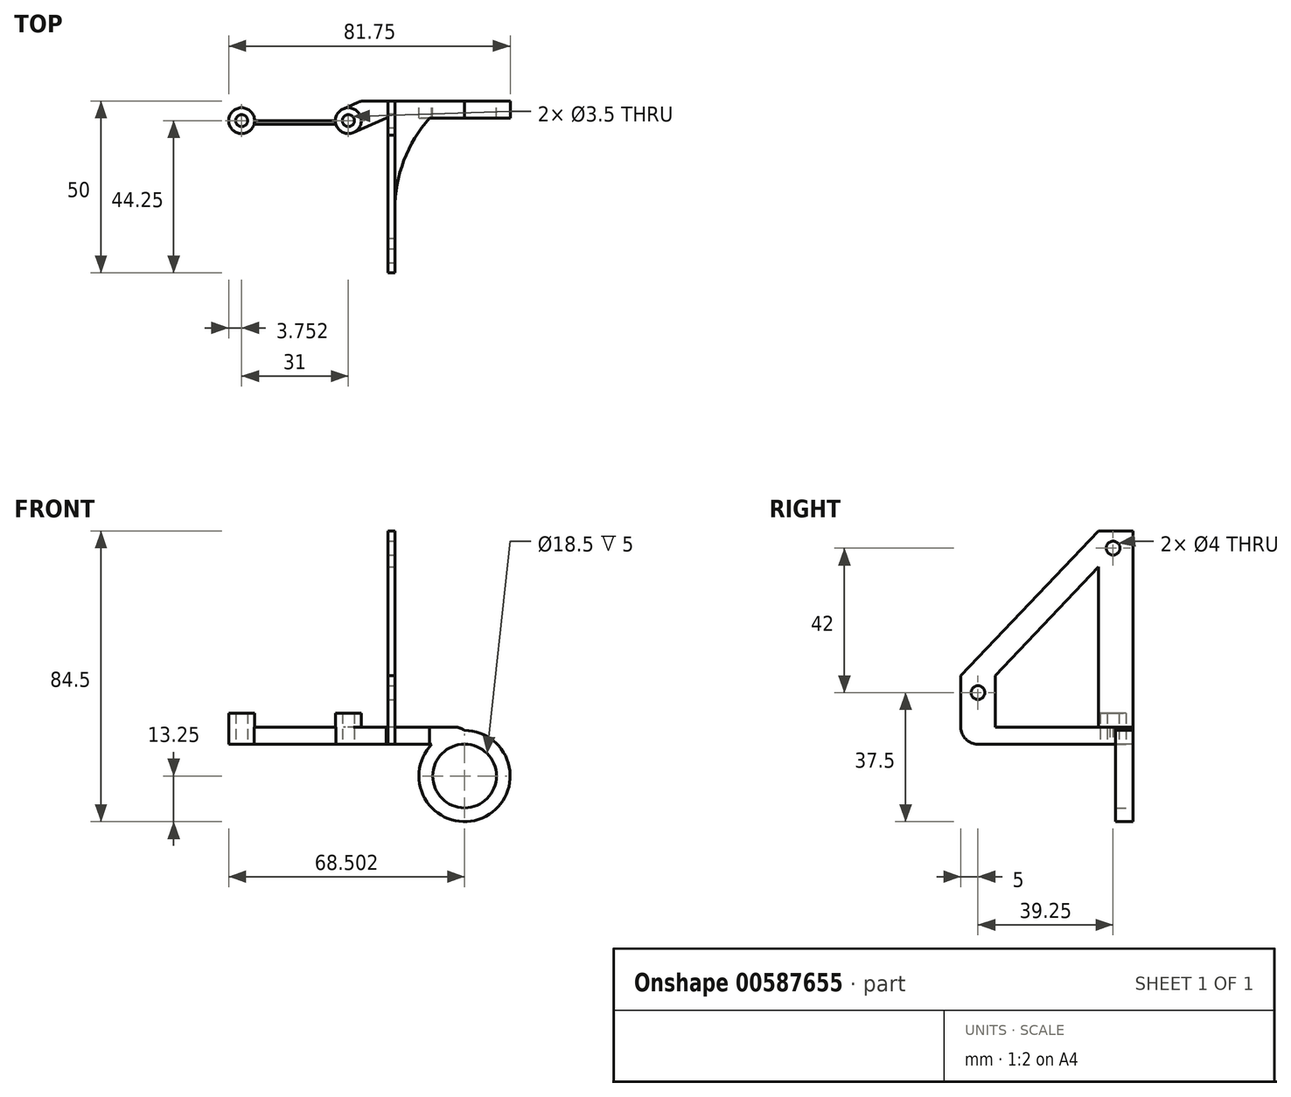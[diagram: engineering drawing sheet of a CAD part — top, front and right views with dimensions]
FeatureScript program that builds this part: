
annotation { "Feature Type Name" : "Feature", "Feature Type Description" : "" }
export const myFeature = defineFeature(function(context is Context, id is Id, definition is map)
    precondition{}
    {
        {
            var Q0;
            Q0=qCreatedBy(makeId("Top.planeOp"),FACE);
            var sketch = newSketch(context, id + "F0", { "sketchPlane" : qUnion([Q0])});
            skCircle(sketch, "E0", {"center": v(-61.06, 0) * mm, "radius": 1.75 * mm});
            skCircle(sketch, "E1", {"center": v(-30.06, 0) * mm, "radius": 1.75 * mm});
            skCircle(sketch, "E2.0", {"center": v(-61.06, 0) * mm, "radius": 3.75 * mm});
            skCircle(sketch, "E3.0", {"center": v(-30.06, 0) * mm, "radius": 3.75 * mm});
            skLineSegment(sketch, "E4", {"start": v(-26.3, 5.75) * mm, "end": v(3.7, 5.75) * mm});
            skLineSegment(sketch, "E5", {"start": v(-26.3, 0) * mm, "end": v(-26.3, 0.75) * mm});
            skLineSegment(sketch, "E6", {"start": v(3.7, 5.75) * mm, "end": v(3.7, 0.75) * mm});
            skPoint(sketch, "E7", {"position": v(-26.3, 0.75) * mm});
            skLineSegment(sketch, "E8.trimOffspring", {"start": v(-26.3, 0.75) * mm, "end": v(3.7, 0.75) * mm});
            skLineSegment(sketch, "E9", {"start": v(-26.3, 0.75) * mm, "end": v(-26.3, 5.75) * mm});
            skPoint(sketch, "E10", {"position": v(-26.3, 5.75) * mm});
            skLineSegment(sketch, "E11", {"start": v(-26.3, 5.75) * mm, "end": v(-31.57, 3.43) * mm});
            skLineSegment(sketch, "E12", {"start": v(-28.55, -3.43) * mm, "end": v(-19.06, 0.75) * mm});
            skLineSegment(sketch, "E13", {"start": v(-57.44, -1) * mm, "end": v(-33.67, -1) * mm});
            skPoint(sketch, "E14", {"position": v(-33.8, 0) * mm});
            skPoint(sketch, "E15", {"position": v(-57.3, 0) * mm});
            skLineSegment(sketch, "E16", {"start": v(-57.3, 0) * mm, "end": v(-33.8, 0) * mm});
            skSolve(sketch);
        }
        {
            var Q0;
            Q0 = qSketchRegion(id + "F0", true);
            extrude(context, id + "F1", {"entities" : qUnion([Q0]), "depth" : 5 * mm, "offsetDistance" : 25 * mm});
        }
        {
            var Q0;
            Q0=makeQuery(id+"F1.opExtrude","SWEPT_FACE",FACE,{"disambiguationData":[OSD([sQuery(id+"F0.wireOp",EDGE,"E4")])]});
            var sketch = newSketch(context, id + "F2", { "sketchPlane" : qUnion([Q0])});
            skPoint(sketch, "E17", {"position": v(-3.7, -9.25) * mm});
            skCircle(sketch, "E18", {"center": v(-3.7, -9.25) * mm, "radius": 9.25 * mm});
            skCircle(sketch, "E19", {"center": v(-3.7, -9.25) * mm, "radius": 13.25 * mm});
            skLineSegment(sketch, "E20", {"start": v(-3.7, 2.5) * mm, "end": v(-3.7, -9.25) * mm});
            skSolve(sketch);
        }
        {
            var Q0;
            Q0 = qSketchRegion(id + "F2", true);
            extrude(context, id + "F3", {"entities" : qUnion([Q0]), "operationType" : NewBodyOperationType.ADD, "depth" : -5 * mm, "offsetDistance" : 25 * mm});
        }
        {
            var Q0;
            Q0=makeQuery(id+"F1.opExtrude","CAP_EDGE",EDGE,{"disambiguationData":[OSD([sQuery(id+"F0.wireOp",EDGE,"E6")])],"isStart":false});
            fillet(context, id + "F4", {"entities" : qUnion([Q0]), "radius" : 5 * mm, "tangentPropagation" : true, "allowEdgeOverflow" : false});
        }
        {
            var Q0;
            Q0=makeQuery(id+"F0.imprint","IMPRINT",FACE,{"disambiguationData":[TD([[makeQuery(id+"F0.imprint","IMPRINT",EDGE,{"derivedFrom":sQuery(id+"F0.wireOp",EDGE,"E0")}),-1.0]])]});
            var Q1;
            Q1=makeQuery(id+"F0.imprint","IMPRINT",FACE,{"disambiguationData":[TD([[makeQuery(id+"F0.imprint","IMPRINT",EDGE,{"derivedFrom":sQuery(id+"F0.wireOp",EDGE,"E1")}),-1.0]])]});
            extrude(context, id + "F5", {"entities" : qUnion([Q0, Q1]), "operationType" : NewBodyOperationType.ADD, "depth" : 9 * mm, "offsetDistance" : 25 * mm});
        }
        {
            var Q0;
            Q0=makeQuery(id+"F1.opExtrude","SWEPT_EDGE",EDGE,{"disambiguationData":[OSD([sQuery(id+"F0.wireOp",EDGE,"E4"),sQuery(id+"F0.wireOp",EDGE,"E9"),sQuery(id+"F0.wireOp",EDGE,"E11")])]});
            fillet(context, id + "F6", {"entities" : qUnion([Q0]), "radius" : 5 * mm, "tangentPropagation" : true, "allowEdgeOverflow" : false});
        }
        {
            var Q0;
            Q0=makeQuery(id+"F3.boolean.opBoolean","MERGE",FACE,{"derivedFrom":[makeQuery(id+"F1.opExtrude","SWEPT_FACE",FACE,{"disambiguationData":[OSD([sQuery(id+"F0.wireOp",EDGE,"E8.trimOffspring")])]}),makeQuery(id+"F3.opExtrude","CAP_FACE",FACE,{"disambiguationData":[OSD([sQuery(id+"F2.wireOp",EDGE,"E18"),sQuery(id+"F2.wireOp",EDGE,"E19")])],"isStart":false})]});
            var sketch = newSketch(context, id + "F7", { "sketchPlane" : qUnion([Q0])});
            skLineSegment(sketch, "E21", {"start": v(-18.56, 0) * mm, "end": v(-18.56, 5) * mm});
            skLineSegment(sketch, "E22", {"start": v(-18.56, 0) * mm, "end": v(-16.56, 0) * mm});
            skLineSegment(sketch, "E23", {"start": v(-16.56, 0) * mm, "end": v(-16.56, 5) * mm});
            skLineSegment(sketch, "E24", {"start": v(-16.56, 5) * mm, "end": v(-18.56, 5) * mm});
            skSolve(sketch);
        }
        {
            var Q0;
            Q0 = qSketchRegion(id + "F7", true);
            extrude(context, id + "F8", {"entities" : qUnion([Q0]), "operationType" : NewBodyOperationType.ADD, "depth" : 45 * mm, "offsetDistance" : 25 * mm});
        }
        {
            var Q0;
            {var subQ0=sQuery(id+"F0.wireOp",EDGE,"E8.trimOffspring");var subQ1=sQuery(id+"F0.wireOp",EDGE,"E6");var subQ2=sQuery(id+"F0.wireOp",EDGE,"E3.0");var subQ3=sQuery(id+"F0.wireOp",EDGE,"E4");var subQ4=sQuery(id+"F0.wireOp",EDGE,"E12");var subQ5=sQuery(id+"F0.wireOp",EDGE,"E13");var subQ6=sQuery(id+"F0.wireOp",EDGE,"E11");var subQ7=sQuery(id+"F0.wireOp",EDGE,"E16");Q0=makeQuery(id+"F8.boolean.opBoolean","MERGE",FACE,{"derivedFrom":[makeQuery(id+"F5.boolean.opBoolean","SPLIT",FACE,{"disambiguationData":[TD([makeQuery(id+"F1.opExtrude","SWEPT_FACE",FACE,{"disambiguationData":[OSD([subQ3])]})])],"derivedFrom":makeQuery(id+"F1.opExtrude","CAP_FACE",FACE,{"disambiguationData":[OSD([sQuery(id+"F0.wireOp",EDGE,"E0"),sQuery(id+"F0.wireOp",EDGE,"E1"),sQuery(id+"F0.wireOp",EDGE,"E2.0"),subQ2,subQ3,subQ1,subQ0,subQ6,subQ4,subQ5,subQ7])],"isStart":false})}),makeQuery(id+"F8.opExtrude","SWEPT_FACE",FACE,{"disambiguationData":[OSD([sQuery(id+"F7.wireOp",EDGE,"E24")])]})]});}
            var sketch = newSketch(context, id + "F9", { "sketchPlane" : qUnion([Q0])});
            skLineSegment(sketch, "E25", {"start": v(-16.56, -44.25) * mm, "end": v(-16.56, -34.25) * mm});
            skLineSegment(sketch, "E26", {"start": v(-16.56, -34.25) * mm, "end": v(-18.56, -34.25) * mm});
            skLineSegment(sketch, "E27", {"start": v(-18.56, -34.25) * mm, "end": v(-18.56, -44.25) * mm});
            skLineSegment(sketch, "E28", {"start": v(-18.56, -44.25) * mm, "end": v(-16.56, -44.25) * mm});
            skSolve(sketch);
        }
        {
            var Q0;
            Q0 = qSketchRegion(id + "F9", true);
            extrude(context, id + "F10", {"entities" : qUnion([Q0]), "operationType" : NewBodyOperationType.ADD, "depth" : 15 * mm, "offsetDistance" : 25 * mm});
        }
        {
            var Q0;
            Q0=makeQuery(id+"F10.boolean.opBoolean","MERGE",FACE,{"derivedFrom":[makeQuery(id+"F8.opExtrude","SWEPT_FACE",FACE,{"disambiguationData":[OSD([sQuery(id+"F7.wireOp",EDGE,"E23")])]}),makeQuery(id+"F10.opExtrude","SWEPT_FACE",FACE,{"disambiguationData":[OSD([sQuery(id+"F9.wireOp",EDGE,"E25")])]})]});
            var sketch = newSketch(context, id + "F11", { "sketchPlane" : qUnion([Q0])});
            skCircle(sketch, "E29", {"center": v(-39.25, 15) * mm, "radius": 2 * mm});
            skLineSegment(sketch, "E30", {"start": v(-44.25, 15) * mm, "end": v(-34.25, 15) * mm});
            skSolve(sketch);
        }
        {
            var Q0;
            Q0 = qSketchRegion(id + "F11", true);
            extrude(context, id + "F12", {"entities" : qUnion([Q0]), "operationType" : NewBodyOperationType.REMOVE, "oppositeDirection" : true, "depth" : 2 * mm, "offsetDistance" : 25 * mm});
        }
        {
            var Q0;
            {var subQ0=sQuery(id+"F0.wireOp",EDGE,"E8.trimOffspring");var subQ1=sQuery(id+"F0.wireOp",EDGE,"E6");var subQ2=sQuery(id+"F0.wireOp",EDGE,"E3.0");var subQ3=sQuery(id+"F0.wireOp",EDGE,"E4");var subQ4=sQuery(id+"F0.wireOp",EDGE,"E12");var subQ5=sQuery(id+"F0.wireOp",EDGE,"E13");var subQ6=sQuery(id+"F0.wireOp",EDGE,"E11");var subQ7=sQuery(id+"F0.wireOp",EDGE,"E16");Q0=makeQuery(id+"F8.boolean.opBoolean","MERGE",FACE,{"derivedFrom":[makeQuery(id+"F5.boolean.opBoolean","SPLIT",FACE,{"disambiguationData":[TD([makeQuery(id+"F1.opExtrude","SWEPT_FACE",FACE,{"disambiguationData":[OSD([subQ3])]})])],"derivedFrom":makeQuery(id+"F1.opExtrude","CAP_FACE",FACE,{"disambiguationData":[OSD([sQuery(id+"F0.wireOp",EDGE,"E0"),sQuery(id+"F0.wireOp",EDGE,"E1"),sQuery(id+"F0.wireOp",EDGE,"E2.0"),subQ2,subQ3,subQ1,subQ0,subQ6,subQ4,subQ5,subQ7])],"isStart":false})}),makeQuery(id+"F8.opExtrude","SWEPT_FACE",FACE,{"disambiguationData":[OSD([sQuery(id+"F7.wireOp",EDGE,"E24")])]})]});}
            var sketch = newSketch(context, id + "F13", { "sketchPlane" : qUnion([Q0])});
            skLineSegment(sketch, "E31", {"start": v(-16.56, -4.25) * mm, "end": v(-16.56, 5.75) * mm});
            skLineSegment(sketch, "E32", {"start": v(-16.56, -4.25) * mm, "end": v(-18.56, -4.25) * mm});
            skLineSegment(sketch, "E33", {"start": v(-18.56, 5.75) * mm, "end": v(-16.56, 5.75) * mm});
            skLineSegment(sketch, "E34", {"start": v(-18.56, 5.75) * mm, "end": v(-18.56, -4.25) * mm});
            skSolve(sketch);
        }
        {
            var Q0;
            Q0 = qSketchRegion(id + "F13", true);
            extrude(context, id + "F14", {"entities" : qUnion([Q0]), "operationType" : NewBodyOperationType.ADD, "depth" : 57 * mm, "offsetDistance" : 25 * mm});
        }
        {
            var Q0;
            Q0=makeQuery(id+"F14.boolean.opBoolean","MERGE",FACE,{"derivedFrom":[makeQuery(id+"F10.boolean.opBoolean","MERGE",FACE,{"derivedFrom":[makeQuery(id+"F8.opExtrude","SWEPT_FACE",FACE,{"disambiguationData":[OSD([sQuery(id+"F7.wireOp",EDGE,"E23")])]}),makeQuery(id+"F10.opExtrude","SWEPT_FACE",FACE,{"disambiguationData":[OSD([sQuery(id+"F9.wireOp",EDGE,"E25")])]})]}),makeQuery(id+"F14.opExtrude","SWEPT_FACE",FACE,{"disambiguationData":[OSD([sQuery(id+"F13.wireOp",EDGE,"E31")])]})]});
            var sketch = newSketch(context, id + "F15", { "sketchPlane" : qUnion([Q0])});
            skCircle(sketch, "E35", {"center": v(0, 57) * mm, "radius": 2 * mm});
            skSolve(sketch);
        }
        {
            var Q0;
            Q0 = qSketchRegion(id + "F15", true);
            extrude(context, id + "F16", {"entities" : qUnion([Q0]), "operationType" : NewBodyOperationType.REMOVE, "oppositeDirection" : true, "depth" : 2 * mm, "offsetDistance" : 25 * mm});
        }
        {
            var Q0;
            Q0=makeQuery(id+"F14.boolean.opBoolean","MERGE",FACE,{"derivedFrom":[makeQuery(id+"F10.boolean.opBoolean","MERGE",FACE,{"derivedFrom":[makeQuery(id+"F8.opExtrude","SWEPT_FACE",FACE,{"disambiguationData":[OSD([sQuery(id+"F7.wireOp",EDGE,"E23")])]}),makeQuery(id+"F10.opExtrude","SWEPT_FACE",FACE,{"disambiguationData":[OSD([sQuery(id+"F9.wireOp",EDGE,"E25")])]})]}),makeQuery(id+"F14.opExtrude","SWEPT_FACE",FACE,{"disambiguationData":[OSD([sQuery(id+"F13.wireOp",EDGE,"E31")])]})]});
            var sketch = newSketch(context, id + "F17", { "sketchPlane" : qUnion([Q0])});
            skLineSegment(sketch, "E36", {"start": v(-4.25, 62) * mm, "end": v(-44.25, 20) * mm});
            skLineSegment(sketch, "E37", {"start": v(-44.25, 20) * mm, "end": v(-34.25, 20) * mm});
            skLineSegment(sketch, "E38", {"start": v(-34.25, 20) * mm, "end": v(-4.25, 51.5) * mm});
            skPoint(sketch, "E39", {"position": v(-4.25, 51.5) * mm});
            skLineSegment(sketch, "E40", {"start": v(-4.25, 51.5) * mm, "end": v(-4.25, 62) * mm});
            skSolve(sketch);
        }
        {
            var Q0;
            Q0 = qSketchRegion(id + "F17", true);
            extrude(context, id + "F18", {"entities" : qUnion([Q0]), "operationType" : NewBodyOperationType.ADD, "depth" : -2 * mm, "offsetDistance" : 25 * mm});
        }
        {
            var Q0;
            Q0=makeQuery(id+"F8.opExtrude","CAP_EDGE",EDGE,{"disambiguationData":[OSD([sQuery(id+"F7.wireOp",EDGE,"E22")])],"isStart":false});
            fillet(context, id + "F19", {"entities" : qUnion([Q0]), "radius" : 5 * mm, "tangentPropagation" : true, "allowEdgeOverflow" : false});
        }
        {
            var Q0;
            Q0=makeQuery(id+"F8.opExtrude","CAP_EDGE",EDGE,{"disambiguationData":[OSD([sQuery(id+"F7.wireOp",EDGE,"E23")])],"isStart":true});
            chamfer(context, id + "F20", {"entities" : qUnion([Q0]), "width" : 10.1 * mm, "tangentPropagation" : true});
        }
        {
            var Q0;
            {var subQ0=sQuery(id+"F7.wireOp",EDGE,"E23");Q0=makeQuery(id+"F20.opChamfer","BLEND_EDGE",EDGE,{"blendedFrom":[makeQuery(id+"F8.opExtrude","CAP_EDGE",EDGE,{"disambiguationData":[OSD([subQ0])],"isStart":true}),makeQuery(id+"F18.boolean.opBoolean","MERGE",FACE,{"derivedFrom":[makeQuery(id+"F14.boolean.opBoolean","MERGE",FACE,{"derivedFrom":[makeQuery(id+"F10.boolean.opBoolean","MERGE",FACE,{"derivedFrom":[makeQuery(id+"F8.opExtrude","SWEPT_FACE",FACE,{"disambiguationData":[OSD([subQ0])]}),makeQuery(id+"F10.opExtrude","SWEPT_FACE",FACE,{"disambiguationData":[OSD([sQuery(id+"F9.wireOp",EDGE,"E25")])]})]}),makeQuery(id+"F14.opExtrude","SWEPT_FACE",FACE,{"disambiguationData":[OSD([sQuery(id+"F13.wireOp",EDGE,"E31")])]})]}),makeQuery(id+"F18.opExtrude","CAP_FACE",FACE,{"disambiguationData":[OSD([sQuery(id+"F17.wireOp",EDGE,"E36"),sQuery(id+"F17.wireOp",EDGE,"E37"),sQuery(id+"F17.wireOp",EDGE,"E38"),sQuery(id+"F17.wireOp",EDGE,"E40")])],"isStart":true})]})],"blendedInto":[makeQuery(id+"F18.boolean.opBoolean","MERGE",FACE,{"derivedFrom":[makeQuery(id+"F14.boolean.opBoolean","MERGE",FACE,{"derivedFrom":[makeQuery(id+"F10.boolean.opBoolean","MERGE",FACE,{"derivedFrom":[makeQuery(id+"F8.opExtrude","SWEPT_FACE",FACE,{"disambiguationData":[OSD([subQ0])]}),makeQuery(id+"F10.opExtrude","SWEPT_FACE",FACE,{"disambiguationData":[OSD([sQuery(id+"F9.wireOp",EDGE,"E25")])]})]}),makeQuery(id+"F14.opExtrude","SWEPT_FACE",FACE,{"disambiguationData":[OSD([sQuery(id+"F13.wireOp",EDGE,"E31")])]})]}),makeQuery(id+"F18.opExtrude","CAP_FACE",FACE,{"disambiguationData":[OSD([sQuery(id+"F17.wireOp",EDGE,"E36"),sQuery(id+"F17.wireOp",EDGE,"E37"),sQuery(id+"F17.wireOp",EDGE,"E38"),sQuery(id+"F17.wireOp",EDGE,"E40")])],"isStart":true})]})]});}
            fillet(context, id + "F21", {"entities" : qUnion([Q0]), "radius" : 40 * mm, "tangentPropagation" : true, "allowEdgeOverflow" : false});
        }
    });
